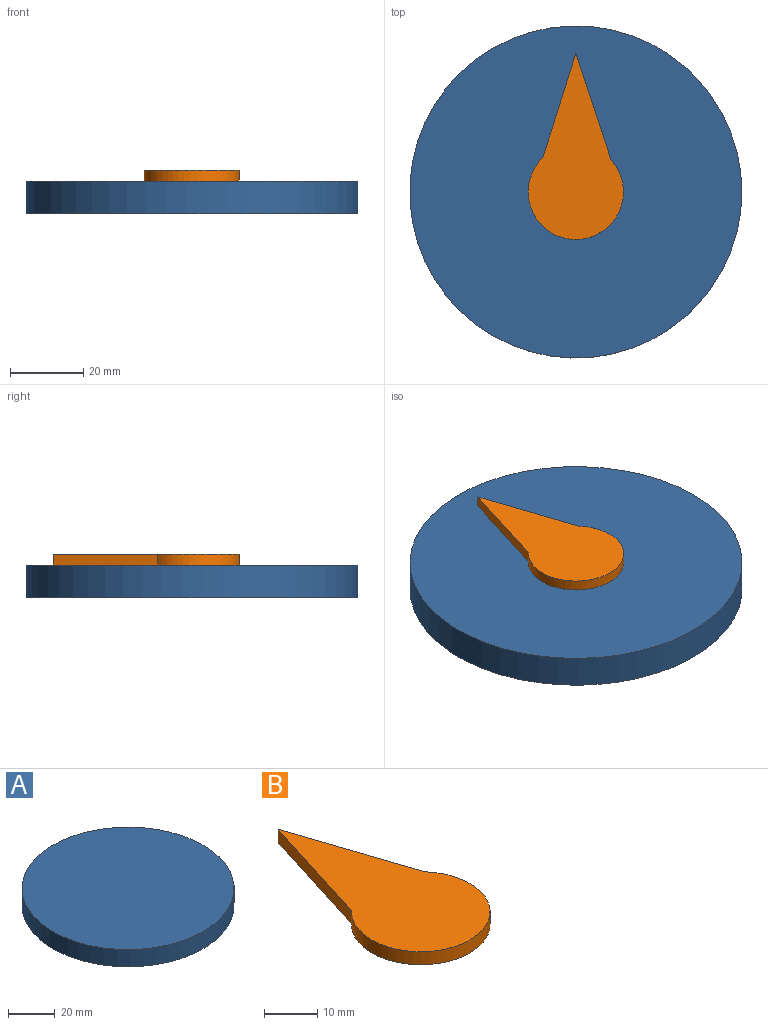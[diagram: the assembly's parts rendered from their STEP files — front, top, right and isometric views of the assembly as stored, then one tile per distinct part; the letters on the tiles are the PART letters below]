
ASSEMBLY  parts=2 mates=1
PART A: 3 faces, bbox 90.9x90.9x9 mm
  f0: cylinder r=45.45mm len=90.91mm, axis (0,0,-1), area 2570.4mm2, adj f1,f2
  f1: plane 90.91x90.91mm, normal (0,0,1), area 6491mm2, adj f0
  f2: plane 90.91x90.91mm, normal (0,0,-1), area 6491mm2, adj f0
PART B: 5 faces, bbox 26.1x51x3 mm
  f0: cylinder r=13.04mm len=26.08mm, axis (0,0,-1), area 183.2mm2, adj f1,f2,f3,f4
  f1: plane 29.25x9.69mm, normal (0.95,0.31,0), area 92.4mm2, adj f0,f2,f3,f4
  f2: plane 28.54x9mm, normal (-0.95,0.3,0), area 89.8mm2, adj f0,f1,f3,f4
  f3: plane 51.02x26.08mm, normal (0,0,1), area 753mm2, adj f0,f1,f2
  f4: plane 51.02x26.08mm, normal (0,0,-1), area 753mm2, adj f0,f1,f2
PLACE A at identity fixed
PLACE B at identity
MATE revolute A.f0 <-> B.f0  axis (0,0,1) through (0,0,9)mm
